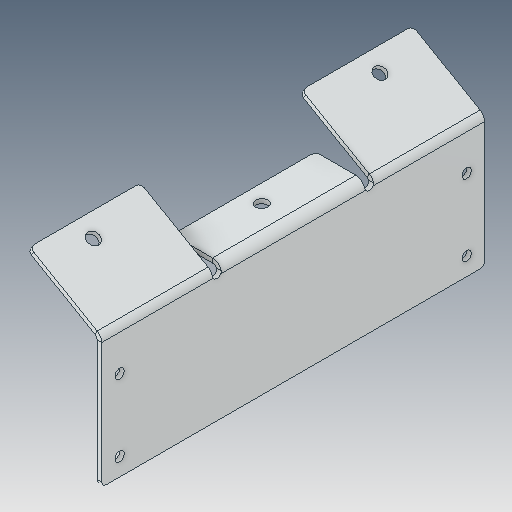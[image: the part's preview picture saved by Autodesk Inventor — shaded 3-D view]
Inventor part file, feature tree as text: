
AUTODESK INVENTOR PART (.ipt)
format: ipt  version: 2023.5 (Build 275446000, 446)  size: 138,752 bytes
history: native  units: in
note: dims shown in document units (in); Inventor stores cm internally (conversion verified against a paired STEP export)
features: fillet x1
ambient origin geometry x8: Origin, YZ Plane, XZ Plane, XY Plane, X Axis, Y Axis, Z Axis, Center Point
bodies: Solid1 (feature_tree)
feature tree (1):
  fillet  "Fillet3"  [1 undecoded]
note: 1 required parameter value undecoded (feature->parameter linkage not recoverable at this tier; creation-order binding heuristic only, values carry confidence <= 0.55)
